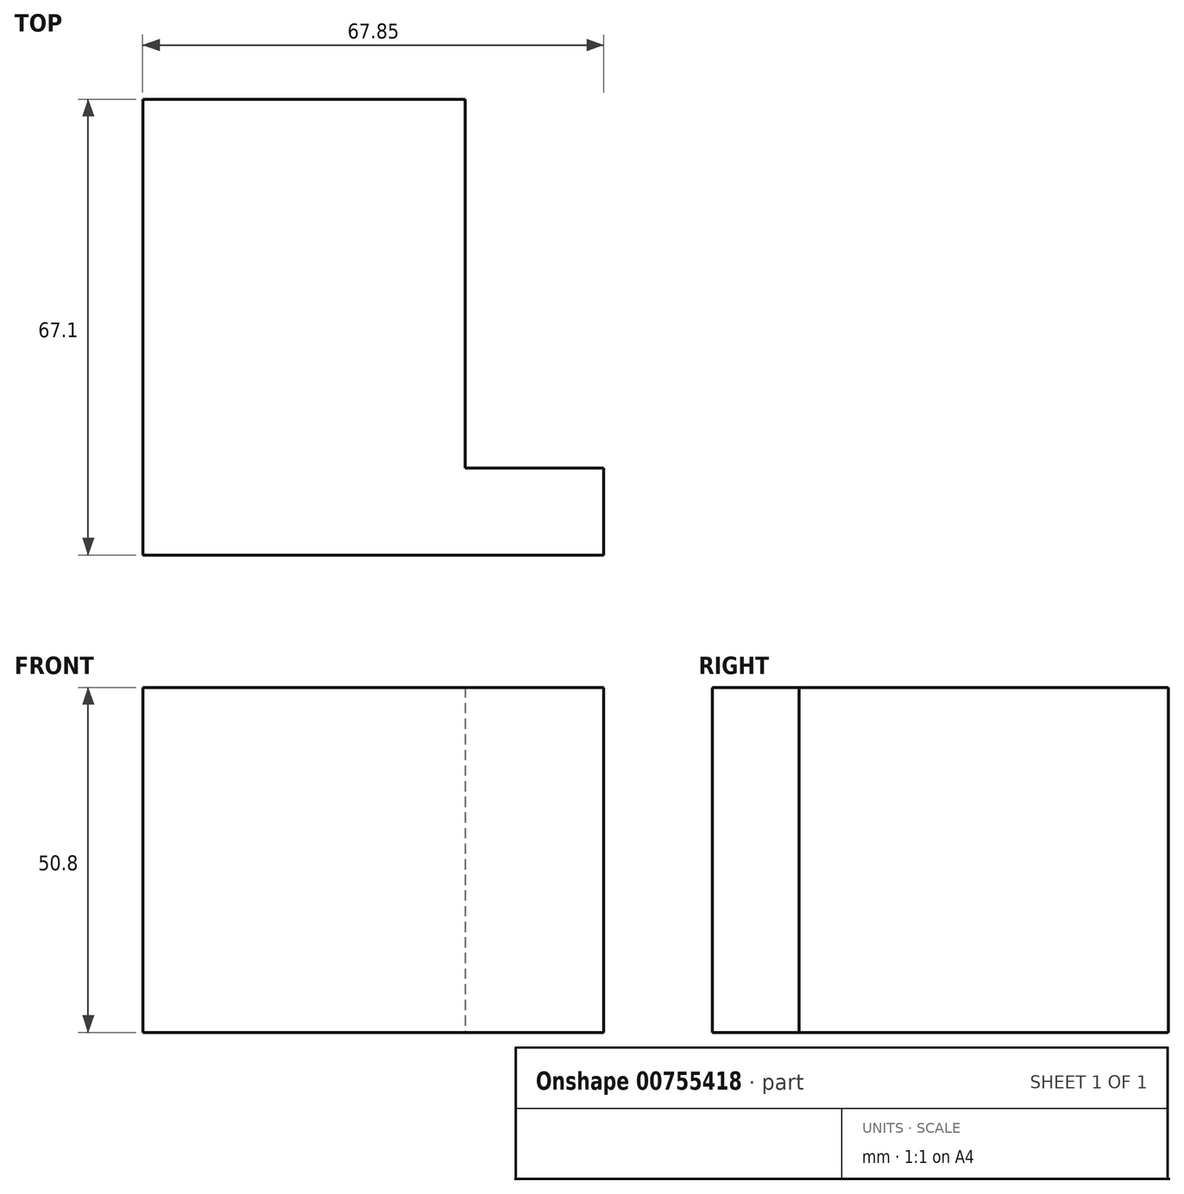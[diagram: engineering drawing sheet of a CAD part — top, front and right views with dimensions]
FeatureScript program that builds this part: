
annotation { "Feature Type Name" : "Feature", "Feature Type Description" : "" }
export const myFeature = defineFeature(function(context is Context, id is Id, definition is map)
    precondition{}
    {
        {
            var Q0;
            Q0=qCreatedBy(makeId("Top.planeOp"),FACE);
            var sketch = newSketch(context, id + "F0", { "sketchPlane" : qUnion([Q0])});
            skLineSegment(sketch, "E0.bottom", {"start": v(-62.18, 39.22) * mm, "end": v(-14.72, 39.22) * mm});
            skLineSegment(sketch, "E0.top", {"start": v(-62.18, -27.88) * mm, "end": v(-14.72, -27.88) * mm});
            skLineSegment(sketch, "E0.left", {"start": v(-62.18, 39.22) * mm, "end": v(-62.18, -27.88) * mm});
            skLineSegment(sketch, "E0.right", {"start": v(-14.72, 39.22) * mm, "end": v(-14.72, -15.1) * mm});
            skLineSegment(sketch, "E1.bottom", {"start": v(-14.72, -27.88) * mm, "end": v(5.67, -27.88) * mm});
            skLineSegment(sketch, "E1.top", {"start": v(-14.72, -15.1) * mm, "end": v(5.67, -15.1) * mm});
            skLineSegment(sketch, "E1.right", {"start": v(5.67, -27.88) * mm, "end": v(5.67, -15.1) * mm});
            skSolve(sketch);
        }
        {
            var Q0;
            Q0 = qSketchRegion(id + "F0", true);
            extrude(context, id + "F1", {"entities" : qUnion([Q0]), "depth" : 50.8 * mm, "offsetDistance" : 25.4 * mm});
        }
    });
